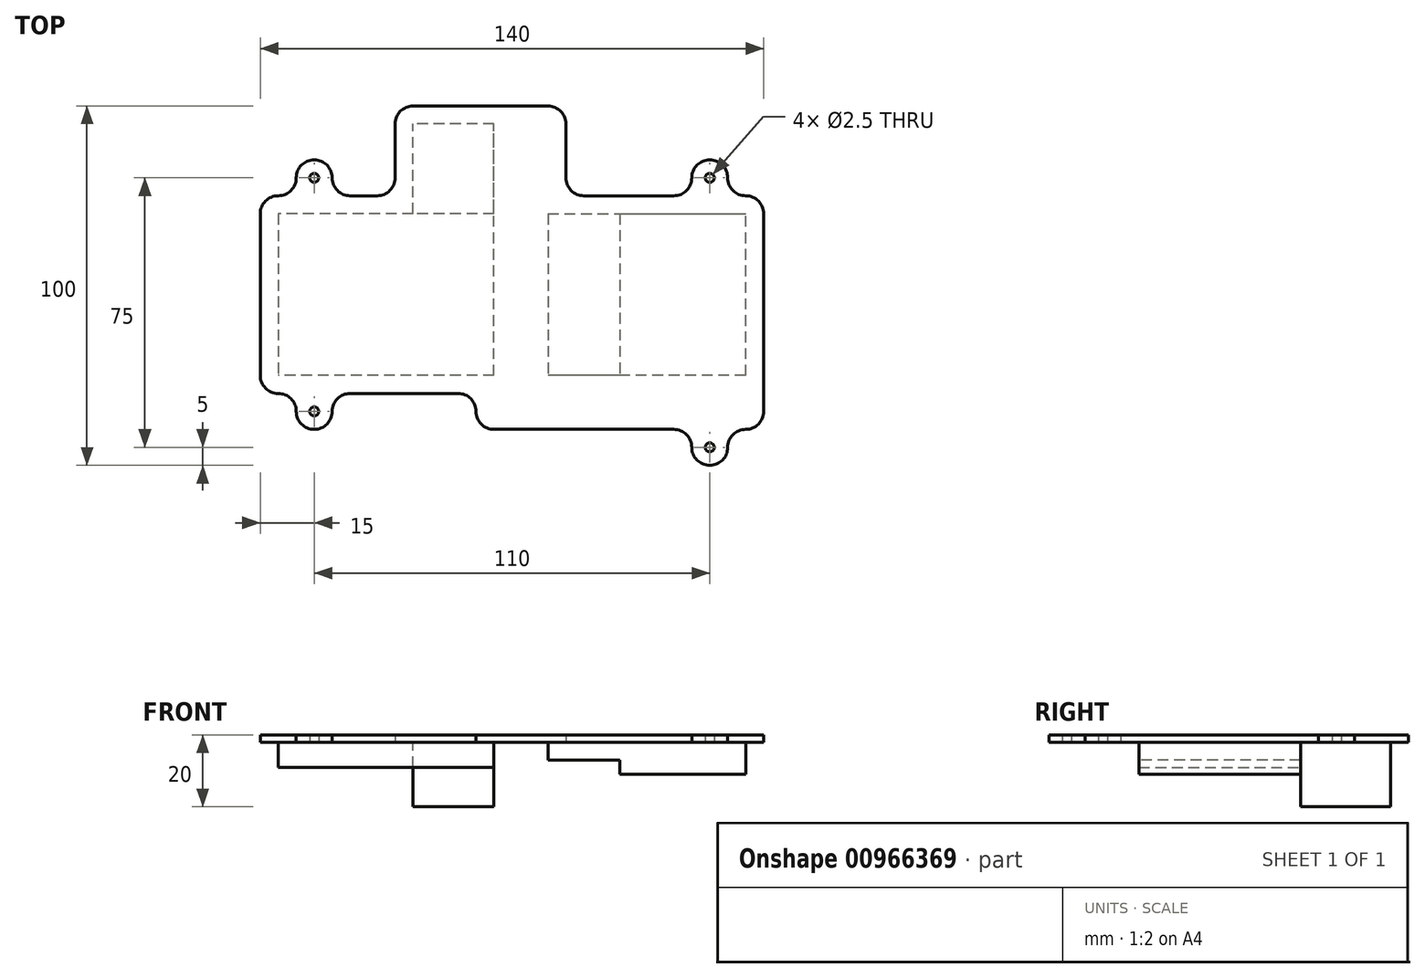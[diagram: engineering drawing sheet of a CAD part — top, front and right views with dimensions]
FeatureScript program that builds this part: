
annotation { "Feature Type Name" : "Feature", "Feature Type Description" : "" }
export const myFeature = defineFeature(function(context is Context, id is Id, definition is map)
    precondition{}
    {
        {
            var Q0;
            Q0=qCreatedBy(makeId("Top.planeOp"),FACE);
            var sketch = newSketch(context, id + "F0", { "sketchPlane" : qUnion([Q0])});
            skLineSegment(sketch, "E0.bottom", {"start": v(0, 0) * mm, "end": v(70, 0) * mm});
            skLineSegment(sketch, "E0.top", {"start": v(0, 55) * mm, "end": v(70, 55) * mm});
            skLineSegment(sketch, "E0.left", {"start": v(0, 0) * mm, "end": v(0, 55) * mm});
            skLineSegment(sketch, "E0.right", {"start": v(70, 0) * mm, "end": v(70, 55) * mm});
            skPoint(sketch, "E1", {"position": v(0, 27.5) * mm});
            skLineSegment(sketch, "E2.bottom", {"start": v(70, 55) * mm, "end": v(-60, 55) * mm});
            skLineSegment(sketch, "E2.top", {"start": v(70, 10) * mm, "end": v(-60, 10) * mm});
            skLineSegment(sketch, "E2.left", {"start": v(70, 55) * mm, "end": v(70, 10) * mm});
            skLineSegment(sketch, "E2.right", {"start": v(-60, 55) * mm, "end": v(-60, 10) * mm});
            skLineSegment(sketch, "E3.bottom", {"start": v(70, 55) * mm, "end": v(35, 55) * mm});
            skLineSegment(sketch, "E3.top", {"start": v(70, 0) * mm, "end": v(35, 0) * mm});
            skLineSegment(sketch, "E3.left", {"start": v(70, 55) * mm, "end": v(70, 0) * mm});
            skLineSegment(sketch, "E3.right", {"start": v(35, 55) * mm, "end": v(35, 0) * mm});
            skLineSegment(sketch, "E4.bottom", {"start": v(35, 55) * mm, "end": v(15, 55) * mm});
            skLineSegment(sketch, "E4.top", {"start": v(35, 0) * mm, "end": v(15, 0) * mm});
            skLineSegment(sketch, "E4.right", {"start": v(15, 55) * mm, "end": v(15, 0) * mm});
            skLineSegment(sketch, "E5.bottom", {"start": v(12.5, 52.5) * mm, "end": v(7.5, 52.5) * mm});
            skLineSegment(sketch, "E5.top", {"start": v(12.5, 40) * mm, "end": v(7.5, 40) * mm});
            skLineSegment(sketch, "E5.left", {"start": v(12.5, 52.5) * mm, "end": v(12.5, 40) * mm});
            skLineSegment(sketch, "E5.right", {"start": v(7.5, 52.5) * mm, "end": v(7.5, 40) * mm});
            skLineSegment(sketch, "E6.bottom", {"start": v(15, 55) * mm, "end": v(-22.5, 55) * mm});
            skLineSegment(sketch, "E6.top", {"start": v(15, 80) * mm, "end": v(-22.5, 80) * mm});
            skLineSegment(sketch, "E6.left", {"start": v(15, 55) * mm, "end": v(15, 80) * mm});
            skLineSegment(sketch, "E6.right", {"start": v(-22.5, 55) * mm, "end": v(-22.5, 80) * mm});
            skLineSegment(sketch, "E7.bottom", {"start": v(15, 40) * mm, "end": v(0, 40) * mm});
            skLineSegment(sketch, "E7.top", {"start": v(15, 80) * mm, "end": v(0, 80) * mm});
            skLineSegment(sketch, "E7.left", {"start": v(15, 40) * mm, "end": v(15, 80) * mm});
            skLineSegment(sketch, "E7.right", {"start": v(0, 40) * mm, "end": v(0, 80) * mm});
            skLineSegment(sketch, "E8.top", {"start": v(15, 10) * mm, "end": v(35, 10) * mm});
            skLineSegment(sketch, "E8.left", {"start": v(15, 5) * mm, "end": v(15, 10) * mm});
            skLineSegment(sketch, "E8.right", {"start": v(35, 5) * mm, "end": v(35, 10) * mm});
            skLineSegment(sketch, "E9.top", {"start": v(35, 55) * mm, "end": v(40, 55) * mm});
            skLineSegment(sketch, "E9.left", {"start": v(35, 5) * mm, "end": v(35, 55) * mm});
            skSolve(sketch);
        }
        {
            var Q0;
            Q0=qCreatedBy(makeId("Top.planeOp"),FACE);
            var sketch = newSketch(context, id + "F1", { "sketchPlane" : qUnion([Q0])});
            skLineSegment(sketch, "E10", {"start": v(75, 0) * mm, "end": v(75, 55) * mm});
            skLineSegment(sketch, "E11", {"start": v(20, 65) * mm, "end": v(20, 80) * mm});
            skLineSegment(sketch, "E12", {"start": v(15, 85) * mm, "end": v(-22.5, 85) * mm});
            skLineSegment(sketch, "E13", {"start": v(-27.5, 80) * mm, "end": v(-27.5, 65) * mm});
            skLineSegment(sketch, "E14", {"start": v(70, -5) * mm, "end": v(70, -5) * mm});
            skLineSegment(sketch, "E15", {"start": v(-65, 55) * mm, "end": v(-65, 10) * mm});
            skLineSegment(sketch, "E16", {"start": v(-5, 0) * mm, "end": v(-5, 0) * mm});
            skPoint(sketch, "E17.visualSharp", {"position": v(-65, 60) * mm});
            skArc(sketch, "E17.filletArc", {"start": v(-60, 60) * mm, "mid": v(-63.54, 58.54) * mm, "end": v(-65, 55) * mm});
            skPoint(sketch, "E18.visualSharp", {"position": v(-65, 5) * mm});
            skArc(sketch, "E18.filletArc", {"start": v(-65, 10) * mm, "mid": v(-63.54, 6.46) * mm, "end": v(-60, 5) * mm});
            skPoint(sketch, "E19.visualSharp", {"position": v(-5, -5) * mm});
            skArc(sketch, "E19.filletArc", {"start": v(-5, 0) * mm, "mid": v(-3.54, -3.54) * mm, "end": v(0, -5) * mm});
            skPoint(sketch, "E20.visualSharp", {"position": v(-5, 5) * mm});
            skArc(sketch, "E20.filletArc", {"start": v(-5, 0) * mm, "mid": v(-6.46, 3.54) * mm, "end": v(-10, 5) * mm});
            skPoint(sketch, "E21.visualSharp", {"position": v(75, -5) * mm});
            skArc(sketch, "E21.filletArc", {"start": v(70, -5) * mm, "mid": v(73.54, -3.54) * mm, "end": v(75, 0) * mm});
            skArc(sketch, "E22.filletArc", {"start": v(75, 55) * mm, "mid": v(73.54, 58.54) * mm, "end": v(70, 60) * mm});
            skPoint(sketch, "E23.visualSharp", {"position": v(20, 85) * mm});
            skArc(sketch, "E23.filletArc", {"start": v(20, 80) * mm, "mid": v(18.54, 83.54) * mm, "end": v(15, 85) * mm});
            skPoint(sketch, "E24.visualSharp", {"position": v(20, 60) * mm});
            skArc(sketch, "E24.filletArc", {"start": v(20, 65) * mm, "mid": v(21.46, 61.46) * mm, "end": v(25, 60) * mm});
            skPoint(sketch, "E25.visualSharp", {"position": v(-27.5, 85) * mm});
            skArc(sketch, "E25.filletArc", {"start": v(-22.5, 85) * mm, "mid": v(-26.04, 83.54) * mm, "end": v(-27.5, 80) * mm});
            skLineSegment(sketch, "E26.top", {"start": v(60, 70) * mm, "end": v(60, 70) * mm});
            skLineSegment(sketch, "E26.left", {"start": v(65, 65) * mm, "end": v(65, 65) * mm});
            skLineSegment(sketch, "E26.right", {"start": v(55, 65) * mm, "end": v(55, 65) * mm});
            skLineSegment(sketch, "E27", {"start": v(70, 60) * mm, "end": v(70, 60) * mm});
            skLineSegment(sketch, "E28", {"start": v(25, 60) * mm, "end": v(50, 60) * mm});
            skArc(sketch, "E29.filletArc", {"start": v(65, 65) * mm, "mid": v(66.46, 61.46) * mm, "end": v(70, 60) * mm});
            skArc(sketch, "E30.filletArc", {"start": v(50, 60) * mm, "mid": v(53.54, 61.46) * mm, "end": v(55, 65) * mm});
            skPoint(sketch, "E31.visualSharp", {"position": v(55, 70) * mm});
            skArc(sketch, "E31.filletArc", {"start": v(60, 70) * mm, "mid": v(56.46, 68.54) * mm, "end": v(55, 65) * mm});
            skPoint(sketch, "E32.visualSharp", {"position": v(65, 70) * mm});
            skArc(sketch, "E32.filletArc", {"start": v(65, 65) * mm, "mid": v(63.54, 68.54) * mm, "end": v(60, 70) * mm});
            skLineSegment(sketch, "E33.bottom", {"start": v(65, -5) * mm, "end": v(55, -5) * mm});
            skLineSegment(sketch, "E33.top", {"start": v(60, -15) * mm, "end": v(60, -15) * mm});
            skLineSegment(sketch, "E33.left", {"start": v(65, -10) * mm, "end": v(65, -10) * mm});
            skLineSegment(sketch, "E33.right", {"start": v(55, -10) * mm, "end": v(55, -10) * mm});
            skArc(sketch, "E34.filletArc", {"start": v(70, -5) * mm, "mid": v(66.46, -6.46) * mm, "end": v(65, -10) * mm});
            skLineSegment(sketch, "E35", {"start": v(50, -5) * mm, "end": v(0, -5) * mm});
            skPoint(sketch, "E36.visualSharp", {"position": v(55, -5) * mm});
            skArc(sketch, "E36.filletArc", {"start": v(55, -10) * mm, "mid": v(53.54, -6.46) * mm, "end": v(50, -5) * mm});
            skPoint(sketch, "E37.visualSharp", {"position": v(55, -15) * mm});
            skArc(sketch, "E37.filletArc", {"start": v(55, -10) * mm, "mid": v(56.46, -13.54) * mm, "end": v(60, -15) * mm});
            skPoint(sketch, "E38.visualSharp", {"position": v(65, -15) * mm});
            skArc(sketch, "E38.filletArc", {"start": v(60, -15) * mm, "mid": v(63.54, -13.54) * mm, "end": v(65, -10) * mm});
            skLineSegment(sketch, "E39.top", {"start": v(-50, 70) * mm, "end": v(-50, 70) * mm});
            skLineSegment(sketch, "E39.left", {"start": v(-55, 65) * mm, "end": v(-55, 65) * mm});
            skLineSegment(sketch, "E39.right", {"start": v(-45, 65) * mm, "end": v(-45, 65) * mm});
            skLineSegment(sketch, "E40", {"start": v(-40, 60) * mm, "end": v(-32.5, 60) * mm});
            skLineSegment(sketch, "E41", {"start": v(-60, 60) * mm, "end": v(-60, 60) * mm});
            skPoint(sketch, "E42.visualSharp", {"position": v(-27.5, 60) * mm});
            skArc(sketch, "E42.filletArc", {"start": v(-32.5, 60) * mm, "mid": v(-28.96, 61.46) * mm, "end": v(-27.5, 65) * mm});
            skArc(sketch, "E43.filletArc", {"start": v(-45, 65) * mm, "mid": v(-43.54, 61.46) * mm, "end": v(-40, 60) * mm});
            skPoint(sketch, "E44.visualSharp", {"position": v(-55, 60) * mm});
            skArc(sketch, "E44.filletArc", {"start": v(-60, 60) * mm, "mid": v(-56.46, 61.46) * mm, "end": v(-55, 65) * mm});
            skPoint(sketch, "E45.visualSharp", {"position": v(-45, 70) * mm});
            skArc(sketch, "E45.filletArc", {"start": v(-45, 65) * mm, "mid": v(-46.46, 68.54) * mm, "end": v(-50, 70) * mm});
            skPoint(sketch, "E46.visualSharp", {"position": v(-55, 70) * mm});
            skArc(sketch, "E46.filletArc", {"start": v(-50, 70) * mm, "mid": v(-53.54, 68.54) * mm, "end": v(-55, 65) * mm});
            skLineSegment(sketch, "E47.top", {"start": v(-50, -5) * mm, "end": v(-50, -5) * mm});
            skLineSegment(sketch, "E47.left", {"start": v(-55, 0) * mm, "end": v(-55, 0) * mm});
            skLineSegment(sketch, "E47.right", {"start": v(-45, 0) * mm, "end": v(-45, 0) * mm});
            skLineSegment(sketch, "E48", {"start": v(-60, 5) * mm, "end": v(-60, 5) * mm});
            skLineSegment(sketch, "E49", {"start": v(-40, 5) * mm, "end": v(-10, 5) * mm});
            skPoint(sketch, "E50.visualSharp", {"position": v(-55, 5) * mm});
            skArc(sketch, "E50.filletArc", {"start": v(-55, 0) * mm, "mid": v(-56.46, 3.54) * mm, "end": v(-60, 5) * mm});
            skPoint(sketch, "E51.visualSharp", {"position": v(-45, 5) * mm});
            skArc(sketch, "E51.filletArc", {"start": v(-40, 5) * mm, "mid": v(-43.54, 3.54) * mm, "end": v(-45, 0) * mm});
            skPoint(sketch, "E52.visualSharp", {"position": v(-45, -5) * mm});
            skArc(sketch, "E52.filletArc", {"start": v(-50, -5) * mm, "mid": v(-46.46, -3.54) * mm, "end": v(-45, 0) * mm});
            skPoint(sketch, "E53.visualSharp", {"position": v(-55, -5) * mm});
            skArc(sketch, "E53.filletArc", {"start": v(-55, 0) * mm, "mid": v(-53.54, -3.54) * mm, "end": v(-50, -5) * mm});
            skLineSegment(sketch, "E54", {"start": v(-22.5, 80) * mm, "end": v(-22.5, 55) * mm});
            skLineSegment(sketch, "E55", {"start": v(-22.5, 55) * mm, "end": v(-60, 55) * mm});
            skLineSegment(sketch, "E56", {"start": v(-60, 10) * mm, "end": v(-60, 55) * mm});
            skLineSegment(sketch, "E57", {"start": v(0, 10) * mm, "end": v(-60, 10) * mm});
            skLineSegment(sketch, "E58", {"start": v(0, 10) * mm, "end": v(0, 0) * mm});
            skLineSegment(sketch, "E59", {"start": v(0, 0) * mm, "end": v(70, 0) * mm});
            skLineSegment(sketch, "E60", {"start": v(70, 0) * mm, "end": v(70, 55) * mm});
            skLineSegment(sketch, "E61", {"start": v(70, 55) * mm, "end": v(15, 55) * mm});
            skLineSegment(sketch, "E62", {"start": v(15, 55) * mm, "end": v(15, 80) * mm});
            skLineSegment(sketch, "E63", {"start": v(-22.5, 80) * mm, "end": v(15, 80) * mm});
            skSolve(sketch);
        }
        {
            var Q0;
            Q0=makeQuery(id+"F1.imprint","IMPRINT",FACE,{"disambiguationData":[TD([[makeQuery(id+"F1.imprint","IMPRINT",EDGE,{"derivedFrom":sQuery(id+"F1.wireOp",EDGE,"E10")}),1.0]])]});
            var Q1;
            Q1=makeQuery(id+"F1.imprint","IMPRINT",FACE,{"disambiguationData":[TD([[makeQuery(id+"F1.imprint","IMPRINT",EDGE,{"derivedFrom":sQuery(id+"F1.wireOp",EDGE,"E55")}),1.0]])]});
            extrude(context, id + "F2", {"entities" : qUnion([Q0, Q1]), "depth" : 2 * mm, "offsetDistance" : 25 * mm});
        }
        {
            var Q0;
            {var subQ5=sQuery(id+"F0.wireOp",EDGE,"E0.top");var subQ7=makeQuery(id+"F0.imprint","IMPRINT",VERTEX,{"derivedFrom":subQ5});Q0=makeQuery(id+"F0.imprint","IMPRINT",FACE,{"disambiguationData":[TD([[makeQuery(id+"F0.imprint","IMPRINT",EDGE,{"disambiguationData":[TD([[subQ7,-1.0]])],"derivedFrom":subQ5}),-1.0]])]});}
            extrude(context, id + "F3", {"entities" : qUnion([Q0]), "operationType" : NewBodyOperationType.ADD, "oppositeDirection" : true, "depth" : 9 * mm, "offsetDistance" : 25 * mm});
        }
        {
            var Q0;
            {var subQ2=sQuery(id+"F0.wireOp",EDGE,"E2.top");var subQ4=sQuery(id+"F0.wireOp",EDGE,"E3.right");var subQ5=makeQuery(id+"F0.imprint","INTERSECT",VERTEX,{"derivedFrom":[subQ2,subQ4]});Q0=makeQuery(id+"F0.imprint","IMPRINT",FACE,{"disambiguationData":[TD([[makeQuery(id+"F0.imprint","IMPRINT",EDGE,{"disambiguationData":[TD([[subQ5,-1.0]])],"derivedFrom":subQ2}),-1.0]])]});}
            extrude(context, id + "F4", {"entities" : qUnion([Q0]), "operationType" : NewBodyOperationType.ADD, "oppositeDirection" : true, "depth" : 5 * mm, "offsetDistance" : 25 * mm});
        }
        {
            var Q0;
            {var subQ0=sQuery(id+"F0.wireOp",EDGE,"E6.right");Q0=makeQuery(id+"F0.imprint","IMPRINT",FACE,{"disambiguationData":[TD([[makeQuery(id+"F0.imprint","IMPRINT",EDGE,{"derivedFrom":subQ0}),-1.0]])]});}
            extrude(context, id + "F5", {"entities" : qUnion([Q0]), "operationType" : NewBodyOperationType.ADD, "oppositeDirection" : true, "depth" : 18 * mm, "offsetDistance" : 25 * mm});
        }
        {
            var Q0;
            {var subQ5=sQuery(id+"F0.wireOp",EDGE,"E2.right");Q0=makeQuery(id+"F0.imprint","IMPRINT",FACE,{"disambiguationData":[TD([[makeQuery(id+"F0.imprint","IMPRINT",EDGE,{"derivedFrom":subQ5}),1.0]])]});}
            extrude(context, id + "F6", {"entities" : qUnion([Q0]), "operationType" : NewBodyOperationType.ADD, "oppositeDirection" : true, "depth" : 7 * mm, "offsetDistance" : 25 * mm});
        }
        {
            var Q0;
            Q0=sQuery(id+"F1.wireOp",VERTEX,"E31.filletArc.center");
            var Q1;
            Q1=sQuery(id+"F1.wireOp",VERTEX,"E45.filletArc.center");
            var Q2;
            Q2=sQuery(id+"F1.wireOp",VERTEX,"E52.filletArc.center");
            var Q3;
            Q3=sQuery(id+"F1.wireOp",VERTEX,"E37.filletArc.center");
            var Q4;
            Q4=makeQuery(id+"F2.opExtrude","SWEPT_BODY",BODY,{"disambiguationData":[OSD([sQuery(id+"F1.wireOp",EDGE,"E10"),sQuery(id+"F1.wireOp",EDGE,"E11"),sQuery(id+"F1.wireOp",EDGE,"E12"),sQuery(id+"F1.wireOp",EDGE,"E13"),sQuery(id+"F1.wireOp",EDGE,"E15"),sQuery(id+"F1.wireOp",EDGE,"E17.filletArc"),sQuery(id+"F1.wireOp",EDGE,"E18.filletArc"),sQuery(id+"F1.wireOp",EDGE,"E19.filletArc"),sQuery(id+"F1.wireOp",EDGE,"E20.filletArc"),sQuery(id+"F1.wireOp",EDGE,"E21.filletArc"),sQuery(id+"F1.wireOp",EDGE,"E22.filletArc"),sQuery(id+"F1.wireOp",EDGE,"E23.filletArc"),sQuery(id+"F1.wireOp",EDGE,"E24.filletArc"),sQuery(id+"F1.wireOp",EDGE,"E25.filletArc"),sQuery(id+"F1.wireOp",EDGE,"E28"),sQuery(id+"F1.wireOp",EDGE,"E29.filletArc"),sQuery(id+"F1.wireOp",EDGE,"E30.filletArc"),sQuery(id+"F1.wireOp",EDGE,"E31.filletArc"),sQuery(id+"F1.wireOp",EDGE,"E32.filletArc"),sQuery(id+"F1.wireOp",EDGE,"E34.filletArc"),sQuery(id+"F1.wireOp",EDGE,"E35"),sQuery(id+"F1.wireOp",EDGE,"E36.filletArc"),sQuery(id+"F1.wireOp",EDGE,"E37.filletArc"),sQuery(id+"F1.wireOp",EDGE,"E38.filletArc"),sQuery(id+"F1.wireOp",EDGE,"E40"),sQuery(id+"F1.wireOp",EDGE,"E42.filletArc"),sQuery(id+"F1.wireOp",EDGE,"E43.filletArc"),sQuery(id+"F1.wireOp",EDGE,"E44.filletArc"),sQuery(id+"F1.wireOp",EDGE,"E45.filletArc"),sQuery(id+"F1.wireOp",EDGE,"E46.filletArc"),sQuery(id+"F1.wireOp",EDGE,"E49"),sQuery(id+"F1.wireOp",EDGE,"E50.filletArc"),sQuery(id+"F1.wireOp",EDGE,"E51.filletArc"),sQuery(id+"F1.wireOp",EDGE,"E52.filletArc"),sQuery(id+"F1.wireOp",EDGE,"E53.filletArc")])]});
            hole(context, id + "F7", {"style" : HoleStyle.SIMPLE, "endStyle" : HoleEndStyle.THROUGH, "oppositeDirection" : true, "holeDiameter" : 2.5 * mm, "majorDiameter" : 5 * mm, "isTappedThrough" : true, "tappedDepth" : 12 * mm, "tapClearance" : 3, "locations" : qUnion([Q0, Q1, Q2, Q3]), "scope" : qUnion([Q4])});
        }
    });
